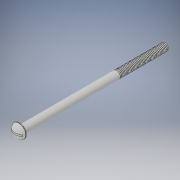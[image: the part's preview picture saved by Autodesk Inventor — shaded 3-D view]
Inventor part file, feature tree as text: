
AUTODESK INVENTOR PART (.ipt)
format: ipt  version: 2018 (Build 220112000, 112)  size: 1,068,032 bytes
history: native  units: in
note: dims shown in document units (in); Inventor stores cm internally (conversion verified against a paired STEP export)
features: extrude x2, other x1, sketch x1
ambient origin geometry x8: Origin, YZ Plane, XZ Plane, XY Plane, X Axis, Y Axis, Z Axis, Center Point
bodies: Solid1 (feature_tree)
feature tree (4):
  other  "91783A846_18-8 SS ROUND HEAD SLOTTED MACHINE SCREW1"
  extrude  "Extrusion1"  [1 undecoded]
  extrude  "Extrude12"  [1 undecoded]
  sketch  "Sketch1"  dims[d0=0.25in d1=0.0in]
note: 2 required parameter values undecoded (feature->parameter linkage not recoverable at this tier; creation-order binding heuristic only, values carry confidence <= 0.55)
